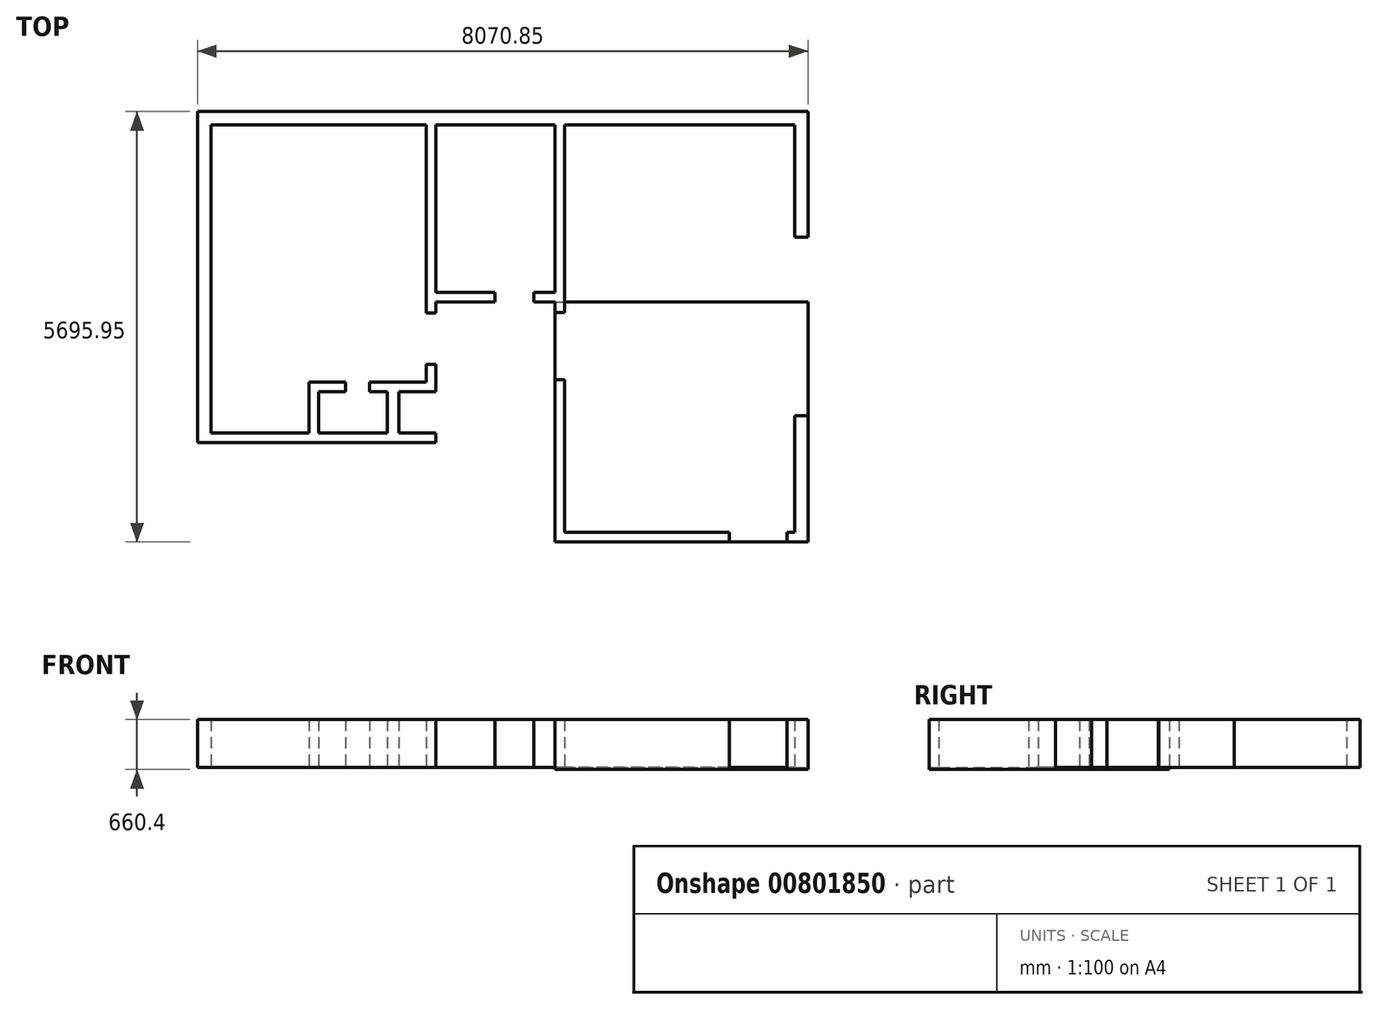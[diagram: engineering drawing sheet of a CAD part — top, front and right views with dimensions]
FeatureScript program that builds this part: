
annotation { "Feature Type Name" : "Feature", "Feature Type Description" : "" }
export const myFeature = defineFeature(function(context is Context, id is Id, definition is map)
    precondition{}
    {
        {
            var Q0;
            Q0=qCreatedBy(makeId("Top.planeOp"),FACE);
            var sketch = newSketch(context, id + "F0", { "sketchPlane" : qUnion([Q0])});
            skLineSegment(sketch, "E0.bottom", {"start": v(0, 0) * mm, "end": v(-101.6, 0) * mm});
            skLineSegment(sketch, "E0.top", {"start": v(0, 5391.15) * mm, "end": v(-3041.65, 5391.15) * mm});
            skLineSegment(sketch, "E0.left", {"start": v(0, 0) * mm, "end": v(0, 1543.05) * mm});
            skLineSegment(sketch, "E0.right", {"start": v(-3041.65, 0) * mm, "end": v(-3041.65, 2019.3) * mm});
            skLineSegment(sketch, "E1", {"start": v(-3041.65, 2019.3) * mm, "end": v(-3168.65, 2019.3) * mm});
            skLineSegment(sketch, "E2", {"start": v(-3168.65, 2019.3) * mm, "end": v(-3168.65, -127) * mm});
            skLineSegment(sketch, "E3", {"start": v(-3168.65, -127) * mm, "end": v(-863.6, -127) * mm});
            skLineSegment(sketch, "E4", {"start": v(-863.6, -127) * mm, "end": v(-863.6, 0) * mm});
            skLineSegment(sketch, "E5", {"start": v(-3041.65, 2908.3) * mm, "end": v(-3168.65, 2908.3) * mm});
            skLineSegment(sketch, "E6", {"start": v(-3168.65, 2908.3) * mm, "end": v(-3168.65, 3048.74) * mm});
            skLineSegment(sketch, "E7", {"start": v(-3168.65, 5568.95) * mm, "end": v(177.8, 5568.95) * mm});
            skLineSegment(sketch, "E8", {"start": v(177.8, 5568.95) * mm, "end": v(177.8, 3905.25) * mm});
            skLineSegment(sketch, "E9", {"start": v(177.8, 3905.25) * mm, "end": v(0, 3905.25) * mm});
            skLineSegment(sketch, "E10", {"start": v(0, 1543.05) * mm, "end": v(177.8, 1543.05) * mm});
            skLineSegment(sketch, "E11", {"start": v(177.8, 1543.05) * mm, "end": v(177.8, -127) * mm});
            skLineSegment(sketch, "E12", {"start": v(177.8, -127) * mm, "end": v(-101.6, -127) * mm});
            skLineSegment(sketch, "E13", {"start": v(-101.6, -127) * mm, "end": v(-101.6, 0) * mm});
            skLineSegment(sketch, "E14", {"start": v(0, 5391.15) * mm, "end": v(177.8, 5391.15) * mm, "construction": true});
            skLineSegment(sketch, "E15", {"start": v(0, 5568.95) * mm, "end": v(0, 5391.15) * mm, "construction": true});
            skLineSegment(sketch, "E16.trimOffspring", {"start": v(-3041.65, 2908.3) * mm, "end": v(-3041.65, 5391.15) * mm});
            skLineSegment(sketch, "E17.trimOffspring", {"start": v(-863.6, 0) * mm, "end": v(-3041.65, 0) * mm});
            skLineSegment(sketch, "E18.trimOffspring", {"start": v(0, 3905.25) * mm, "end": v(0, 5391.15) * mm});
            skLineSegment(sketch, "E19.bottom", {"start": v(-7715.25, 5391.15) * mm, "end": v(-4870.45, 5391.15) * mm});
            skLineSegment(sketch, "E19.top", {"start": v(-7715.25, 1314.45) * mm, "end": v(-6419.85, 1314.45) * mm});
            skLineSegment(sketch, "E19.left", {"start": v(-7715.25, 5391.15) * mm, "end": v(-7715.25, 1314.45) * mm});
            skLineSegment(sketch, "E19.right", {"start": v(-4870.45, 5391.15) * mm, "end": v(-4870.45, 2901.95) * mm});
            skLineSegment(sketch, "E20", {"start": v(-6419.85, 1314.45) * mm, "end": v(-6419.85, 1987.55) * mm});
            skLineSegment(sketch, "E21", {"start": v(-6419.85, 1987.55) * mm, "end": v(-5938.34, 1987.55) * mm});
            skLineSegment(sketch, "E22", {"start": v(-5384.1, 1860.55) * mm, "end": v(-5384.1, 1314.45) * mm});
            skLineSegment(sketch, "E23.0", {"start": v(-7893.05, 5568.95) * mm, "end": v(-7893.05, 1187.45) * mm});
            skLineSegment(sketch, "E23.1", {"start": v(-7893.05, 5568.95) * mm, "end": v(-3168.65, 5568.95) * mm});
            skLineSegment(sketch, "E24", {"start": v(-3168.65, 5391.15) * mm, "end": v(-4743.45, 5391.15) * mm});
            skLineSegment(sketch, "E25", {"start": v(-4743.45, 5391.15) * mm, "end": v(-4743.45, 3175.74) * mm});
            skLineSegment(sketch, "E26", {"start": v(-3168.65, 3048.74) * mm, "end": v(-3448.14, 3048.74) * mm});
            skLineSegment(sketch, "E27", {"start": v(-3448.14, 3048.74) * mm, "end": v(-3448.14, 3175.74) * mm});
            skLineSegment(sketch, "E28", {"start": v(-3448.14, 3175.74) * mm, "end": v(-3168.65, 3175.74) * mm});
            skLineSegment(sketch, "E29", {"start": v(-4870.45, 5391.15) * mm, "end": v(-4743.45, 5391.15) * mm, "construction": true});
            skLineSegment(sketch, "E30.trimOffspring", {"start": v(-3168.65, 3175.74) * mm, "end": v(-3168.65, 5391.15) * mm});
            skLineSegment(sketch, "E31", {"start": v(-4743.45, 3175.74) * mm, "end": v(-3962.38, 3175.74) * mm});
            skLineSegment(sketch, "E32", {"start": v(-3962.38, 3175.74) * mm, "end": v(-3962.38, 3048.74) * mm});
            skLineSegment(sketch, "E33", {"start": v(-3962.38, 3048.74) * mm, "end": v(-4743.45, 3048.74) * mm});
            skLineSegment(sketch, "E34", {"start": v(-4743.45, 3048.74) * mm, "end": v(-4743.45, 2901.95) * mm});
            skLineSegment(sketch, "E35", {"start": v(-4743.45, 2901.95) * mm, "end": v(-4870.45, 2901.95) * mm});
            skLineSegment(sketch, "E36", {"start": v(-4870.45, 2226.25) * mm, "end": v(-4743.45, 2226.25) * mm});
            skLineSegment(sketch, "E37.trimOffspring", {"start": v(-4870.45, 2226.25) * mm, "end": v(-4870.45, 1987.55) * mm});
            skLineSegment(sketch, "E38", {"start": v(-4743.45, 2226.25) * mm, "end": v(-4743.45, 1860.55) * mm});
            skLineSegment(sketch, "E39.0", {"start": v(-6292.85, 1314.45) * mm, "end": v(-6292.85, 1860.55) * mm});
            skLineSegment(sketch, "E39.1", {"start": v(-6292.85, 1860.55) * mm, "end": v(-5938.34, 1860.55) * mm});
            skLineSegment(sketch, "E40", {"start": v(-5938.34, 1860.55) * mm, "end": v(-5938.34, 1987.55) * mm});
            skLineSegment(sketch, "E41", {"start": v(-5617.84, 1987.55) * mm, "end": v(-5617.84, 1860.55) * mm});
            skLineSegment(sketch, "E42", {"start": v(-5617.84, 1860.55) * mm, "end": v(-5384.1, 1860.55) * mm});
            skLineSegment(sketch, "E43", {"start": v(-4743.45, 1860.55) * mm, "end": v(-5230, 1860.55) * mm});
            skLineSegment(sketch, "E44", {"start": v(-5230, 1860.55) * mm, "end": v(-5230, 1314.45) * mm});
            skLineSegment(sketch, "E45.trimOffspring", {"start": v(-5617.84, 1987.55) * mm, "end": v(-4870.45, 1987.55) * mm});
            skLineSegment(sketch, "E46", {"start": v(-7893.05, 1187.45) * mm, "end": v(-4743.45, 1187.45) * mm});
            skLineSegment(sketch, "E47", {"start": v(-4743.45, 1187.45) * mm, "end": v(-4743.45, 1314.45) * mm});
            skLineSegment(sketch, "E48", {"start": v(-7715.25, 5391.15) * mm, "end": v(-7893.05, 5391.15) * mm, "construction": true});
            skLineSegment(sketch, "E49.trimOffspring", {"start": v(-5230, 1314.45) * mm, "end": v(-4743.45, 1314.45) * mm});
            skLineSegment(sketch, "E50", {"start": v(-5384.1, 1314.45) * mm, "end": v(-5230, 1314.45) * mm, "construction": true});
            skLineSegment(sketch, "E51.trimOffspring", {"start": v(-6292.85, 1314.45) * mm, "end": v(-5384.1, 1314.45) * mm});
            skSolve(sketch);
        }
        {
            var Q0;
            Q0=qCreatedBy(makeId("Top.planeOp"),FACE);
            var sketch = newSketch(context, id + "F1", { "sketchPlane" : qUnion([Q0])});
            skLineSegment(sketch, "E52.bottom", {"start": v(-3168.65, 3048.74) * mm, "end": v(177.8, 3048.74) * mm});
            skLineSegment(sketch, "E52.top", {"start": v(-3168.65, -127) * mm, "end": v(177.8, -127) * mm});
            skLineSegment(sketch, "E52.left", {"start": v(-3168.65, 3048.74) * mm, "end": v(-3168.65, -127) * mm});
            skLineSegment(sketch, "E52.right", {"start": v(177.8, 3048.74) * mm, "end": v(177.8, -127) * mm});
            skPoint(sketch, "E53", {"position": v(177.8, -0.19) * mm});
            skSolve(sketch);
        }
        {
            var Q0;
            Q0 = qSketchRegion(id + "F1", true);
            extrude(context, id + "F2", {"entities" : qUnion([Q0]), "oppositeDirection" : true, "depth" : 25.4 * mm, "offsetDistance" : 25.4 * mm});
        }
        {
            var Q0;
            Q0 = qSketchRegion(id + "F0", true);
            extrude(context, id + "F3", {"entities" : qUnion([Q0]), "operationType" : NewBodyOperationType.ADD, "depth" : 635 * mm, "offsetDistance" : 25.4 * mm});
        }
    });
